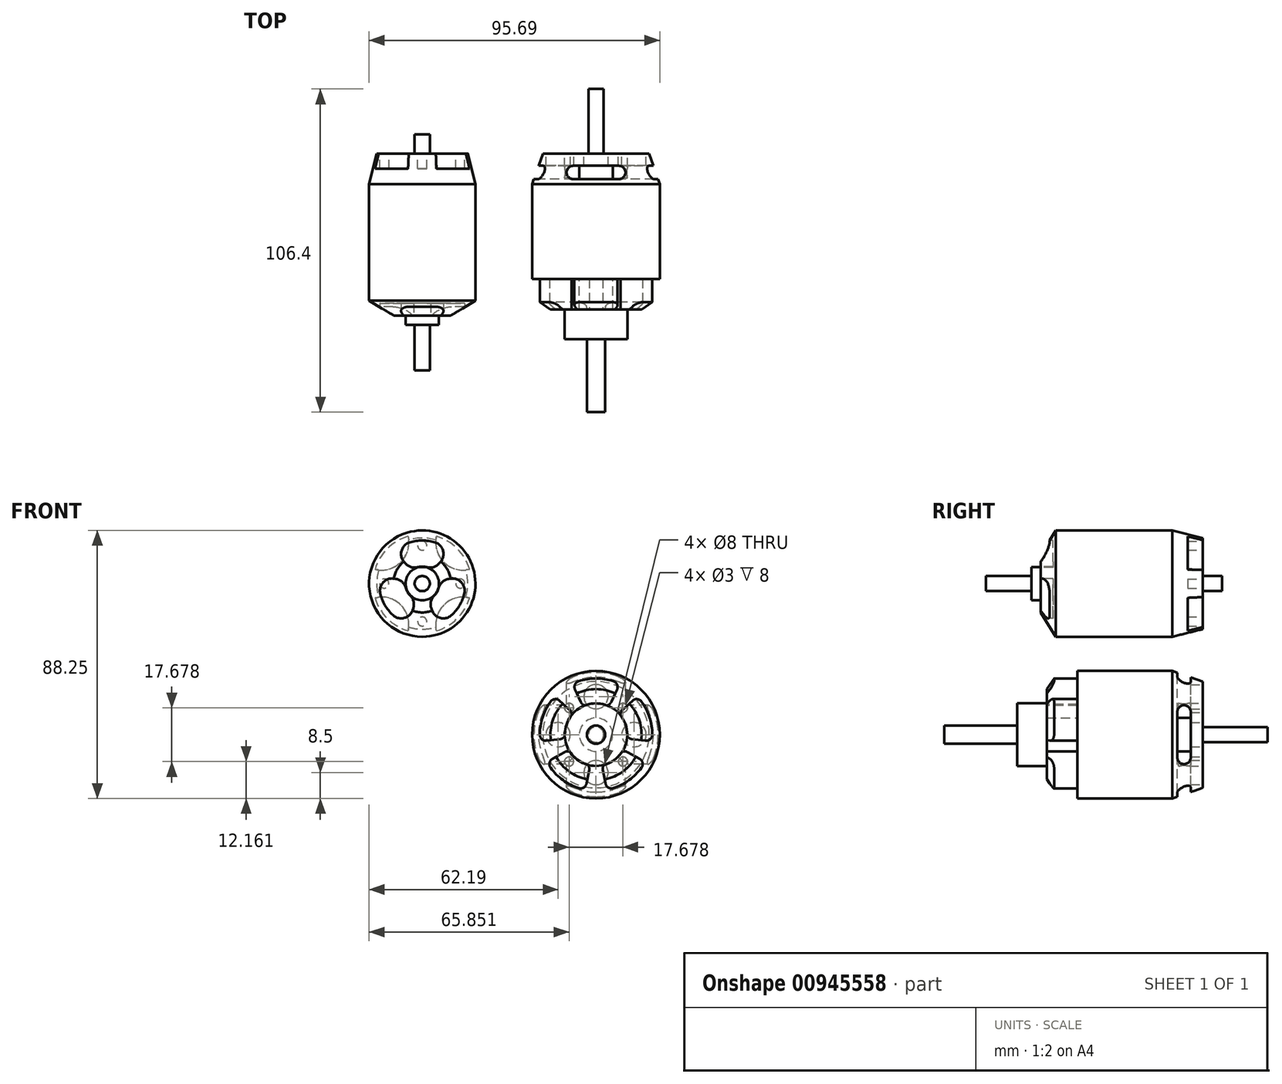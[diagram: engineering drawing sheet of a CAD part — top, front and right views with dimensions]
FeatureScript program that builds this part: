
annotation { "Feature Type Name" : "Feature", "Feature Type Description" : "" }
export const myFeature = defineFeature(function(context is Context, id is Id, definition is map)
    precondition{}
    {
        {
            var Q0;
            Q0=qCreatedBy(makeId("Front.planeOp"),FACE);
            var sketch = newSketch(context, id + "F0", { "sketchPlane" : qUnion([Q0])});
            skCircle(sketch, "E0", {"center": v(0, 0) * mm, "radius": 21 * mm});
            skSolve(sketch);
        }
        {
            var Q0;
            Q0 = qSketchRegion(id + "F0", true);
            extrude(context, id + "F1", {"entities" : qUnion([Q0]), "depth" : 51.3 * mm, "offsetDistance" : 25 * mm});
        }
        {
            var Q0;
            Q0=makeQuery(id+"F1.opExtrude","CAP_FACE",FACE,{"disambiguationData":[OSD([sQuery(id+"F0.wireOp",EDGE,"E0")])],"isStart":false});
            var sketch = newSketch(context, id + "F2", { "sketchPlane" : qUnion([Q0])});
            skArc(sketch, "E1", {"start": v(-2.66, 9.64) * mm, "mid": v(0, 10) * mm, "end": v(2.66, 9.64) * mm});
            skArc(sketch, "E2", {"start": v(-5.73, 17.6) * mm, "mid": v(0, 18.5) * mm, "end": v(5.73, 17.6) * mm});
            skLineSegment(sketch, "E3", {"start": v(-6.92, 14.84) * mm, "end": v(-5, 10.72) * mm});
            skLineSegment(sketch, "E4", {"start": v(-4.23, 9.06) * mm, "end": v(0, 0) * mm, "construction": true});
            skLineSegment(sketch, "E5", {"start": v(5, 10.72) * mm, "end": v(6.92, 14.84) * mm});
            skLineSegment(sketch, "E6", {"start": v(4.23, 9.06) * mm, "end": v(0, 0) * mm, "construction": true});
            skPoint(sketch, "E7.visualSharp", {"position": v(-7.82, 16.77) * mm});
            skArc(sketch, "E7.filletArc", {"start": v(-5.73, 17.6) * mm, "mid": v(-6.94, 16.49) * mm, "end": v(-6.92, 14.84) * mm});
            skPoint(sketch, "E8.visualSharp", {"position": v(7.82, 16.77) * mm});
            skArc(sketch, "E8.filletArc", {"start": v(6.92, 14.84) * mm, "mid": v(6.94, 16.49) * mm, "end": v(5.73, 17.6) * mm});
            skPoint(sketch, "E9.visualSharp", {"position": v(4.23, 9.06) * mm});
            skArc(sketch, "E9.filletArc", {"start": v(2.66, 9.64) * mm, "mid": v(4.03, 9.75) * mm, "end": v(5, 10.72) * mm});
            skPoint(sketch, "E10.visualSharp", {"position": v(-4.23, 9.06) * mm});
            skArc(sketch, "E10.filletArc", {"start": v(-5, 10.72) * mm, "mid": v(-4.03, 9.75) * mm, "end": v(-2.66, 9.64) * mm});
            skArc(sketch, "E11.1.0", {"start": v(-9.99, 0.45) * mm, "mid": v(-9.51, 3.1) * mm, "end": v(-8.35, 5.5) * mm});
            skArc(sketch, "E11.1.1", {"start": v(-11.74, -1.44) * mm, "mid": v(-10.52, -0.82) * mm, "end": v(-9.99, 0.45) * mm});
            skLineSegment(sketch, "E11.1.2", {"start": v(-16.26, -2) * mm, "end": v(-11.74, -1.44) * mm});
            skArc(sketch, "E11.1.3", {"start": v(-18.5, -0.01) * mm, "mid": v(-17.82, -1.5) * mm, "end": v(-16.26, -2) * mm});
            skArc(sketch, "E11.1.4", {"start": v(-18.5, -0.01) * mm, "mid": v(-17.6, 5.72) * mm, "end": v(-14.96, 10.88) * mm});
            skArc(sketch, "E11.1.5", {"start": v(-11.98, 11.17) * mm, "mid": v(-13.53, 11.7) * mm, "end": v(-14.96, 10.88) * mm});
            skLineSegment(sketch, "E11.1.6", {"start": v(-8.65, 8.07) * mm, "end": v(-11.98, 11.17) * mm});
            skArc(sketch, "E11.1.7", {"start": v(-8.35, 5.5) * mm, "mid": v(-8.03, 6.84) * mm, "end": v(-8.65, 8.07) * mm});
            skArc(sketch, "E11.2.0", {"start": v(-3.52, -9.36) * mm, "mid": v(-5.88, -8.1) * mm, "end": v(-7.82, -6.24) * mm});
            skArc(sketch, "E11.2.1", {"start": v(-2.26, -11.61) * mm, "mid": v(-2.48, -10.26) * mm, "end": v(-3.52, -9.36) * mm});
            skLineSegment(sketch, "E11.2.2", {"start": v(-3.13, -16.08) * mm, "end": v(-2.26, -11.61) * mm});
            skArc(sketch, "E11.2.3", {"start": v(-5.7, -17.6) * mm, "mid": v(-4.07, -17.42) * mm, "end": v(-3.13, -16.08) * mm});
            skArc(sketch, "E11.2.4", {"start": v(-5.7, -17.6) * mm, "mid": v(-10.87, -14.97) * mm, "end": v(-14.97, -10.86) * mm});
            skArc(sketch, "E11.2.5", {"start": v(-14.32, -7.94) * mm, "mid": v(-15.3, -9.26) * mm, "end": v(-14.97, -10.86) * mm});
            skLineSegment(sketch, "E11.2.6", {"start": v(-10.35, -5.74) * mm, "end": v(-14.32, -7.94) * mm});
            skArc(sketch, "E11.2.7", {"start": v(-7.82, -6.24) * mm, "mid": v(-9, -5.52) * mm, "end": v(-10.35, -5.74) * mm});
            skArc(sketch, "E11.3.0", {"start": v(7.82, -6.24) * mm, "mid": v(5.88, -8.1) * mm, "end": v(3.52, -9.36) * mm});
            skArc(sketch, "E11.3.1", {"start": v(10.35, -5.74) * mm, "mid": v(9, -5.52) * mm, "end": v(7.82, -6.24) * mm});
            skLineSegment(sketch, "E11.3.2", {"start": v(14.32, -7.94) * mm, "end": v(10.35, -5.74) * mm});
            skArc(sketch, "E11.3.3", {"start": v(14.97, -10.86) * mm, "mid": v(15.3, -9.26) * mm, "end": v(14.32, -7.94) * mm});
            skArc(sketch, "E11.3.4", {"start": v(14.97, -10.86) * mm, "mid": v(10.87, -14.97) * mm, "end": v(5.7, -17.6) * mm});
            skArc(sketch, "E11.3.5", {"start": v(3.13, -16.08) * mm, "mid": v(4.07, -17.42) * mm, "end": v(5.7, -17.6) * mm});
            skLineSegment(sketch, "E11.3.6", {"start": v(2.26, -11.61) * mm, "end": v(3.13, -16.08) * mm});
            skArc(sketch, "E11.3.7", {"start": v(3.52, -9.36) * mm, "mid": v(2.48, -10.26) * mm, "end": v(2.26, -11.61) * mm});
            skArc(sketch, "E11.4.0", {"start": v(8.35, 5.5) * mm, "mid": v(9.51, 3.1) * mm, "end": v(9.99, 0.45) * mm});
            skArc(sketch, "E11.4.1", {"start": v(8.65, 8.07) * mm, "mid": v(8.03, 6.84) * mm, "end": v(8.35, 5.5) * mm});
            skLineSegment(sketch, "E11.4.2", {"start": v(11.98, 11.17) * mm, "end": v(8.65, 8.07) * mm});
            skArc(sketch, "E11.4.3", {"start": v(14.96, 10.88) * mm, "mid": v(13.53, 11.7) * mm, "end": v(11.98, 11.17) * mm});
            skArc(sketch, "E11.4.4", {"start": v(14.96, 10.88) * mm, "mid": v(17.6, 5.72) * mm, "end": v(18.5, -0.01) * mm});
            skArc(sketch, "E11.4.5", {"start": v(16.26, -2) * mm, "mid": v(17.82, -1.5) * mm, "end": v(18.5, -0.01) * mm});
            skLineSegment(sketch, "E11.4.6", {"start": v(11.74, -1.44) * mm, "end": v(16.26, -2) * mm});
            skArc(sketch, "E11.4.7", {"start": v(9.99, 0.45) * mm, "mid": v(10.52, -0.82) * mm, "end": v(11.74, -1.44) * mm});
            skSolve(sketch);
        }
        {
            var Q0;
            Q0=makeQuery(id+"F1.opExtrude","CAP_EDGE",EDGE,{"disambiguationData":[OSD([sQuery(id+"F0.wireOp",EDGE,"E0")])],"isStart":false});
            chamfer(context, id + "F3", {"entities" : qUnion([Q0]), "chamferType" : ChamferType.TWO_OFFSETS, "width1" : 6 * mm, "oppositeDirection" : false, "width2" : 4 * mm, "tangentPropagation" : true});
        }
        {
            var Q0;
            Q0=makeQuery(id+"F1.opExtrude","CAP_EDGE",EDGE,{"disambiguationData":[OSD([sQuery(id+"F0.wireOp",EDGE,"E0")])],"isStart":true});
            chamfer(context, id + "F4", {"entities" : qUnion([Q0]), "chamferType" : ChamferType.TWO_OFFSETS, "width1" : 10 * mm, "oppositeDirection" : false, "width2" : 3.5 * mm, "tangentPropagation" : true});
        }
        {
            var Q0;
            Q0=makeQuery(id+"F2.imprint","IMPRINT",FACE,{"disambiguationData":[TD([[makeQuery(id+"F2.imprint","IMPRINT",EDGE,{"derivedFrom":sQuery(id+"F2.wireOp",EDGE,"E11.1.0")}),1.0]])]});
            var Q1;
            Q1=makeQuery(id+"F2.imprint","IMPRINT",FACE,{"disambiguationData":[TD([[makeQuery(id+"F2.imprint","IMPRINT",EDGE,{"derivedFrom":sQuery(id+"F2.wireOp",EDGE,"E1")}),1.0]])]});
            var Q2;
            Q2=makeQuery(id+"F2.imprint","IMPRINT",FACE,{"disambiguationData":[TD([[makeQuery(id+"F2.imprint","IMPRINT",EDGE,{"derivedFrom":sQuery(id+"F2.wireOp",EDGE,"E11.4.0")}),1.0]])]});
            var Q3;
            Q3=makeQuery(id+"F2.imprint","IMPRINT",FACE,{"disambiguationData":[TD([[makeQuery(id+"F2.imprint","IMPRINT",EDGE,{"derivedFrom":sQuery(id+"F2.wireOp",EDGE,"E11.3.0")}),1.0]])]});
            var Q4;
            Q4=makeQuery(id+"F2.imprint","IMPRINT",FACE,{"disambiguationData":[TD([[makeQuery(id+"F2.imprint","IMPRINT",EDGE,{"derivedFrom":sQuery(id+"F2.wireOp",EDGE,"E11.2.0")}),1.0]])]});
            extrude(context, id + "F5", {"entities" : qUnion([Q0, Q1, Q2, Q3, Q4]), "operationType" : NewBodyOperationType.REMOVE, "oppositeDirection" : true, "depth" : 10 * mm, "offsetDistance" : 25 * mm});
        }
        {
            var Q0;
            Q0=makeQuery(id+"F1.opExtrude","CAP_FACE",FACE,{"disambiguationData":[OSD([sQuery(id+"F0.wireOp",EDGE,"E0")])],"isStart":true});
            var sketch = newSketch(context, id + "F6", { "sketchPlane" : qUnion([Q0])});
            skCircle(sketch, "E12", {"center": v(0, 12.5) * mm, "radius": 4 * mm});
            skCircle(sketch, "E13", {"center": v(8.84, 8.84) * mm, "radius": 1.5 * mm});
            skLineSegment(sketch, "E14", {"start": v(0, 0) * mm, "end": v(8.84, 8.84) * mm, "construction": true});
            skCircle(sketch, "E15.1.0", {"center": v(-12.5, 0) * mm, "radius": 4 * mm});
            skCircle(sketch, "E15.1.1", {"center": v(-8.84, 8.84) * mm, "radius": 1.5 * mm});
            skCircle(sketch, "E15.2.0", {"center": v(0, -12.5) * mm, "radius": 4 * mm});
            skCircle(sketch, "E15.2.1", {"center": v(-8.84, -8.84) * mm, "radius": 1.5 * mm});
            skCircle(sketch, "E15.3.0", {"center": v(12.5, 0) * mm, "radius": 4 * mm});
            skCircle(sketch, "E15.3.1", {"center": v(8.84, -8.84) * mm, "radius": 1.5 * mm});
            skPoint(sketch, "E15.center", {"position": v(0, 0) * mm});
            skSolve(sketch);
        }
        {
            var Q0;
            Q0 = qSketchRegion(id + "F6", true);
            extrude(context, id + "F7", {"entities" : qUnion([Q0]), "operationType" : NewBodyOperationType.REMOVE, "oppositeDirection" : true, "depth" : 8 * mm, "offsetDistance" : 25 * mm});
        }
        {
            var Q0;
            Q0=makeQuery(id+"F1.opExtrude","CAP_FACE",FACE,{"disambiguationData":[OSD([sQuery(id+"F0.wireOp",EDGE,"E0")])],"isStart":false});
            var sketch = newSketch(context, id + "F8", { "sketchPlane" : qUnion([Q0])});
            skCircle(sketch, "E16", {"center": v(0, 0) * mm, "radius": 5.5 * mm});
            skSolve(sketch);
        }
        {
            var Q0;
            Q0=makeQuery(id+"F1.opExtrude","CAP_FACE",FACE,{"disambiguationData":[OSD([sQuery(id+"F0.wireOp",EDGE,"E0")])],"isStart":true});
            var sketch = newSketch(context, id + "F9", { "sketchPlane" : qUnion([Q0])});
            skCircle(sketch, "E17", {"center": v(0, 0) * mm, "radius": 2.5 * mm});
            skSolve(sketch);
        }
        {
            var Q0;
            Q0 = qSketchRegion(id + "F9", true);
            extrude(context, id + "F10", {"entities" : qUnion([Q0]), "operationType" : NewBodyOperationType.ADD, "depth" : 21.3 * mm, "offsetDistance" : 25 * mm});
        }
        {
            var Q0;
            Q0=qCreatedBy(makeId("Right.planeOp"),FACE);
            var sketch = newSketch(context, id + "F11", { "sketchPlane" : qUnion([Q0])});
            skLineSegment(sketch, "E18", {"start": v(-4, 7.5) * mm, "end": v(-4, -7.5) * mm});
            skLineSegment(sketch, "E19", {"start": v(-8.4, 7.5) * mm, "end": v(-8.4, -7.5) * mm});
            skArc(sketch, "E20", {"start": v(-4, -7.5) * mm, "mid": v(-6.2, -9.7) * mm, "end": v(-8.4, -7.5) * mm});
            skArc(sketch, "E21", {"start": v(-4, 7.5) * mm, "mid": v(-6.2, 9.7) * mm, "end": v(-8.4, 7.5) * mm});
            skSolve(sketch);
        }
        {
            var Q0;
            Q0 = qSketchRegion(id + "F11", true);
            extrude(context, id + "F12", {"entities" : qUnion([Q0]), "operationType" : NewBodyOperationType.REMOVE, "endBound" : BoundingType.THROUGH_ALL, "depth" : 50 * mm, "offsetDistance" : 25 * mm, "hasSecondDirection" : true, "secondDirectionBound" : SecondDirectionBoundingType.THROUGH_ALL, "secondDirectionOppositeDirection" : true, "secondDirectionDepth" : 25 * mm});
        }
        {
            var Q0;
            Q0=qCreatedBy(makeId("Top.planeOp"),FACE);
            var sketch = newSketch(context, id + "F13", { "sketchPlane" : qUnion([Q0])});
            skLineSegment(sketch, "E22", {"start": v(-7.5, -4) * mm, "end": v(7.5, -4) * mm});
            skLineSegment(sketch, "E23", {"start": v(-7.5, -8.4) * mm, "end": v(7.5, -8.4) * mm});
            skArc(sketch, "E24", {"start": v(7.5, -4) * mm, "mid": v(9.7, -6.2) * mm, "end": v(7.5, -8.4) * mm});
            skArc(sketch, "E25", {"start": v(-7.5, -4) * mm, "mid": v(-9.7, -6.2) * mm, "end": v(-7.5, -8.4) * mm});
            skSolve(sketch);
        }
        {
            var Q0;
            Q0 = qSketchRegion(id + "F13", true);
            extrude(context, id + "F14", {"entities" : qUnion([Q0]), "operationType" : NewBodyOperationType.REMOVE, "oppositeDirection" : true, "depth" : 25 * mm, "offsetDistance" : 25 * mm, "hasSecondDirection" : true, "secondDirectionOppositeDirection" : false, "secondDirectionDepth" : 25 * mm});
        }
        {
            var Q0;
            Q0 = qSketchRegion(id + "F8", true);
            extrude(context, id + "F15", {"entities" : qUnion([Q0]), "operationType" : NewBodyOperationType.ADD, "depth" : 7 * mm, "offsetDistance" : 25 * mm, "hasSecondDirection" : true, "secondDirectionOppositeDirection" : true, "secondDirectionDepth" : 50 * mm});
        }
        {
            var Q0;
            Q0=makeQuery(id+"F1.opExtrude","CAP_FACE",FACE,{"disambiguationData":[OSD([sQuery(id+"F0.wireOp",EDGE,"E0")])],"isStart":false});
            var sketch = newSketch(context, id + "F16", { "sketchPlane" : qUnion([Q0])});
            skCircle(sketch, "E26", {"center": v(0, -8) * mm, "radius": 1 * mm});
            skLineSegment(sketch, "E27", {"start": v(0, -8) * mm, "end": v(0, 0) * mm, "construction": true});
            skCircle(sketch, "E28.1.0", {"center": v(6.93, 4) * mm, "radius": 1 * mm});
            skCircle(sketch, "E28.2.0", {"center": v(-6.93, 4) * mm, "radius": 1 * mm});
            skPoint(sketch, "E28.center", {"position": v(0, 0) * mm});
            skSolve(sketch);
        }
        {
            var Q0;
            Q0 = qSketchRegion(id + "F16", true);
            extrude(context, id + "F17", {"entities" : qUnion([Q0]), "operationType" : NewBodyOperationType.REMOVE, "oppositeDirection" : true, "depth" : 3 * mm, "offsetDistance" : 25 * mm});
        }
        {
            var Q0;
            Q0=makeQuery(id+"F1.opExtrude","CAP_FACE",FACE,{"disambiguationData":[OSD([sQuery(id+"F0.wireOp",EDGE,"E0")])],"isStart":false});
            var sketch = newSketch(context, id + "F18", { "sketchPlane" : qUnion([Q0])});
            skCircle(sketch, "E29", {"center": v(0, 0) * mm, "radius": 10.3 * mm});
            skCircle(sketch, "E30", {"center": v(0, 0) * mm, "radius": 5.5 * mm});
            skSolve(sketch);
        }
        {
            var Q0;
            Q0 = qSketchRegion(id + "F18", true);
            extrude(context, id + "F19", {"entities" : qUnion([Q0]), "depth" : 7 * mm, "offsetDistance" : 25 * mm});
        }
        {
            var Q0;
            Q0=makeQuery(id+"F19.opExtrude","CAP_FACE",FACE,{"disambiguationData":[OSD([sQuery(id+"F18.wireOp",EDGE,"E29"),sQuery(id+"F18.wireOp",EDGE,"E30")])],"isStart":false});
            var sketch = newSketch(context, id + "F20", { "sketchPlane" : qUnion([Q0])});
            skCircle(sketch, "E31", {"center": v(0, 0) * mm, "radius": 10.3 * mm});
            skSolve(sketch);
        }
        {
            var Q0;
            Q0 = qSketchRegion(id + "F20", true);
            extrude(context, id + "F21", {"entities" : qUnion([Q0]), "operationType" : NewBodyOperationType.ADD, "depth" : 2.8 * mm, "offsetDistance" : 25 * mm});
        }
        {
            var Q0;
            Q0=makeQuery(id+"F21.opExtrude","CAP_FACE",FACE,{"disambiguationData":[OSD([sQuery(id+"F20.wireOp",EDGE,"E31")])],"isStart":false});
            var sketch = newSketch(context, id + "F22", { "sketchPlane" : qUnion([Q0])});
            skCircle(sketch, "E32", {"center": v(0, 0) * mm, "radius": 3 * mm});
            skSolve(sketch);
        }
        {
            var Q0;
            Q0 = qSketchRegion(id + "F22", true);
            extrude(context, id + "F23", {"entities" : qUnion([Q0]), "operationType" : NewBodyOperationType.ADD, "depth" : 24 * mm, "offsetDistance" : 25 * mm});
        }
        {
            var Q0;
            Q0=qCreatedBy(makeId("Front.planeOp"),FACE);
            var sketch = newSketch(context, id + "F24", { "sketchPlane" : qUnion([Q0])});
            skCircle(sketch, "E33", {"center": v(-57.2, 49.75) * mm, "radius": 17.5 * mm});
            skSolve(sketch);
        }
        {
            var Q0;
            Q0 = qSketchRegion(id + "F24", true);
            extrude(context, id + "F25", {"entities" : qUnion([Q0]), "depth" : 53.35 * mm, "offsetDistance" : 25 * mm});
        }
        {
            var Q0;
            Q0=makeQuery(id+"F25.opExtrude","CAP_EDGE",EDGE,{"disambiguationData":[OSD([sQuery(id+"F24.wireOp",EDGE,"E33")])],"isStart":false});
            chamfer(context, id + "F26", {"entities" : qUnion([Q0]), "chamferType" : ChamferType.TWO_OFFSETS, "width1" : 8 * mm, "oppositeDirection" : false, "width2" : 5 * mm, "tangentPropagation" : true});
        }
        {
            var Q0;
            Q0=makeQuery(id+"F25.opExtrude","CAP_EDGE",EDGE,{"disambiguationData":[OSD([sQuery(id+"F24.wireOp",EDGE,"E33")])],"isStart":true});
            chamfer(context, id + "F27", {"entities" : qUnion([Q0]), "chamferType" : ChamferType.TWO_OFFSETS, "width1" : 10 * mm, "oppositeDirection" : false, "width2" : 2.5 * mm, "tangentPropagation" : true});
        }
        {
            var Q0;
            Q0=makeQuery(id+"F25.opExtrude","CAP_FACE",FACE,{"disambiguationData":[OSD([sQuery(id+"F24.wireOp",EDGE,"E33")])],"isStart":false});
            var sketch = newSketch(context, id + "F28", { "sketchPlane" : qUnion([Q0])});
            skArc(sketch, "E34", {"start": v(-61.32, 63.34) * mm, "mid": v(-57.2, 63.95) * mm, "end": v(-53.06, 63.34) * mm});
            skArc(sketch, "E35", {"start": v(-58.68, 55.15) * mm, "mid": v(-57.2, 55.35) * mm, "end": v(-55.7, 55.15) * mm});
            skLineSegment(sketch, "E36", {"start": v(-63.22, 56.94) * mm, "end": v(-62.8, 56.44) * mm});
            skLineSegment(sketch, "E37", {"start": v(-57.2, 49.75) * mm, "end": v(-60.8, 54.04) * mm, "construction": true});
            skLineSegment(sketch, "E38", {"start": v(-57.2, 49.75) * mm, "end": v(-53.6, 54.04) * mm, "construction": true});
            skLineSegment(sketch, "E39", {"start": v(-51.16, 56.94) * mm, "end": v(-51.58, 56.44) * mm});
            skPoint(sketch, "E40.visualSharp", {"position": v(-66.32, 60.63) * mm});
            skArc(sketch, "E40.filletArc", {"start": v(-61.32, 63.34) * mm, "mid": v(-64, 60.65) * mm, "end": v(-63.22, 56.94) * mm});
            skPoint(sketch, "E41.visualSharp", {"position": v(-60.8, 54.04) * mm});
            skArc(sketch, "E41.filletArc", {"start": v(-62.8, 56.44) * mm, "mid": v(-60.93, 55.19) * mm, "end": v(-58.68, 55.15) * mm});
            skPoint(sketch, "E42.visualSharp", {"position": v(-53.6, 54.04) * mm});
            skArc(sketch, "E42.filletArc", {"start": v(-55.7, 55.15) * mm, "mid": v(-53.46, 55.19) * mm, "end": v(-51.58, 56.44) * mm});
            skPoint(sketch, "E43.visualSharp", {"position": v(-48.06, 60.63) * mm});
            skArc(sketch, "E43.filletArc", {"start": v(-51.16, 56.94) * mm, "mid": v(-50.39, 60.65) * mm, "end": v(-53.06, 63.34) * mm});
            skArc(sketch, "E44.1.0", {"start": v(-61.12, 45.77) * mm, "mid": v(-62.04, 46.95) * mm, "end": v(-62.6, 48.34) * mm});
            skArc(sketch, "E44.1.1", {"start": v(-60.18, 41.55) * mm, "mid": v(-60.03, 43.8) * mm, "end": v(-61.12, 45.77) * mm});
            skLineSegment(sketch, "E44.1.2", {"start": v(-60.4, 40.94) * mm, "end": v(-60.18, 41.55) * mm});
            skArc(sketch, "E44.1.3", {"start": v(-66.9, 39.38) * mm, "mid": v(-63.23, 38.41) * mm, "end": v(-60.4, 40.94) * mm});
            skArc(sketch, "E44.1.4", {"start": v(-66.9, 39.38) * mm, "mid": v(-69.49, 42.65) * mm, "end": v(-71.02, 46.54) * mm});
            skArc(sketch, "E44.1.5", {"start": v(-66.43, 51.38) * mm, "mid": v(-70.03, 50.2) * mm, "end": v(-71.02, 46.54) * mm});
            skLineSegment(sketch, "E44.1.6", {"start": v(-66.43, 51.38) * mm, "end": v(-65.79, 51.27) * mm});
            skArc(sketch, "E44.1.7", {"start": v(-62.6, 48.34) * mm, "mid": v(-63.77, 50.27) * mm, "end": v(-65.79, 51.27) * mm});
            skArc(sketch, "E44.2.0", {"start": v(-51.77, 48.34) * mm, "mid": v(-52.34, 46.95) * mm, "end": v(-53.26, 45.77) * mm});
            skArc(sketch, "E44.2.1", {"start": v(-48.6, 51.27) * mm, "mid": v(-50.61, 50.27) * mm, "end": v(-51.77, 48.34) * mm});
            skLineSegment(sketch, "E44.2.2", {"start": v(-47.95, 51.38) * mm, "end": v(-48.6, 51.27) * mm});
            skArc(sketch, "E44.2.3", {"start": v(-43.36, 46.54) * mm, "mid": v(-44.35, 50.2) * mm, "end": v(-47.95, 51.38) * mm});
            skArc(sketch, "E44.2.4", {"start": v(-43.36, 46.54) * mm, "mid": v(-44.9, 42.65) * mm, "end": v(-47.5, 39.38) * mm});
            skArc(sketch, "E44.2.5", {"start": v(-53.98, 40.94) * mm, "mid": v(-51.15, 38.41) * mm, "end": v(-47.5, 39.38) * mm});
            skLineSegment(sketch, "E44.2.6", {"start": v(-53.98, 40.94) * mm, "end": v(-54.2, 41.55) * mm});
            skArc(sketch, "E44.2.7", {"start": v(-53.26, 45.77) * mm, "mid": v(-54.35, 43.8) * mm, "end": v(-54.2, 41.55) * mm});
            skSolve(sketch);
        }
        {
            var Q0;
            Q0 = qSketchRegion(id + "F28", true);
            extrude(context, id + "F29", {"entities" : qUnion([Q0]), "operationType" : NewBodyOperationType.REMOVE, "oppositeDirection" : true, "depth" : 4 * mm, "offsetDistance" : 25 * mm});
        }
        {
            var Q0;
            Q0=makeQuery(id+"F25.opExtrude","CAP_FACE",FACE,{"disambiguationData":[OSD([sQuery(id+"F24.wireOp",EDGE,"E33")])],"isStart":false});
            var sketch = newSketch(context, id + "F30", { "sketchPlane" : qUnion([Q0])});
            skCircle(sketch, "E45", {"center": v(-57.2, 49.75) * mm, "radius": 5.5 * mm});
            skSolve(sketch);
        }
        {
            var Q0;
            Q0 = qSketchRegion(id + "F30", true);
            extrude(context, id + "F31", {"entities" : qUnion([Q0]), "operationType" : NewBodyOperationType.ADD, "depth" : 3 * mm, "offsetDistance" : 25 * mm});
        }
        {
            var Q0;
            Q0=makeQuery(id+"F31.opExtrude","CAP_FACE",FACE,{"disambiguationData":[OSD([sQuery(id+"F30.wireOp",EDGE,"E45")])],"isStart":false});
            var sketch = newSketch(context, id + "F32", { "sketchPlane" : qUnion([Q0])});
            skCircle(sketch, "E46", {"center": v(-57.2, 49.75) * mm, "radius": 2.5 * mm});
            skSolve(sketch);
        }
        {
            var Q0;
            Q0 = qSketchRegion(id + "F32", true);
            extrude(context, id + "F33", {"entities" : qUnion([Q0]), "operationType" : NewBodyOperationType.ADD, "depth" : 15 * mm, "offsetDistance" : 25 * mm});
        }
        {
            var Q0;
            Q0=makeQuery(id+"F25.opExtrude","CAP_FACE",FACE,{"disambiguationData":[OSD([sQuery(id+"F24.wireOp",EDGE,"E33")])],"isStart":true});
            var sketch = newSketch(context, id + "F34", { "sketchPlane" : qUnion([Q0])});
            skCircle(sketch, "E47", {"center": v(57.2, 49.75) * mm, "radius": 2.5 * mm});
            skSolve(sketch);
        }
        {
            var Q0;
            Q0 = qSketchRegion(id + "F34", true);
            extrude(context, id + "F35", {"entities" : qUnion([Q0]), "operationType" : NewBodyOperationType.ADD, "depth" : 6.3 * mm, "offsetDistance" : 25 * mm});
        }
        {
            var Q0;
            Q0=makeQuery(id+"F25.opExtrude","CAP_FACE",FACE,{"disambiguationData":[OSD([sQuery(id+"F24.wireOp",EDGE,"E33")])],"isStart":true});
            var sketch = newSketch(context, id + "F36", { "sketchPlane" : qUnion([Q0])});
            skCircle(sketch, "E48", {"center": v(57.2, 62.25) * mm, "radius": 1.5 * mm});
            skCircle(sketch, "E49", {"center": v(70.63, 63.19) * mm, "radius": 9 * mm});
            skLineSegment(sketch, "E50", {"start": v(57.2, 62.25) * mm, "end": v(57.2, 49.75) * mm, "construction": true});
            skLineSegment(sketch, "E51", {"start": v(57.2, 49.75) * mm, "end": v(70.63, 63.19) * mm, "construction": true});
            skPoint(sketch, "E52.center", {"position": v(57.2, 49.75) * mm});
            skCircle(sketch, "E53.1.0", {"center": v(43.76, 63.19) * mm, "radius": 9 * mm});
            skCircle(sketch, "E53.1.1", {"center": v(44.7, 49.75) * mm, "radius": 1.5 * mm});
            skCircle(sketch, "E53.2.0", {"center": v(43.76, 36.32) * mm, "radius": 9 * mm});
            skCircle(sketch, "E53.2.1", {"center": v(57.2, 37.25) * mm, "radius": 1.5 * mm});
            skCircle(sketch, "E53.3.0", {"center": v(70.63, 36.32) * mm, "radius": 9 * mm});
            skCircle(sketch, "E53.3.1", {"center": v(69.7, 49.75) * mm, "radius": 1.5 * mm});
            skSolve(sketch);
        }
        {
            var Q0;
            Q0 = qSketchRegion(id + "F36", true);
            extrude(context, id + "F37", {"entities" : qUnion([Q0]), "operationType" : NewBodyOperationType.REMOVE, "oppositeDirection" : true, "depth" : 5 * mm, "offsetDistance" : 25 * mm});
        }
    });
